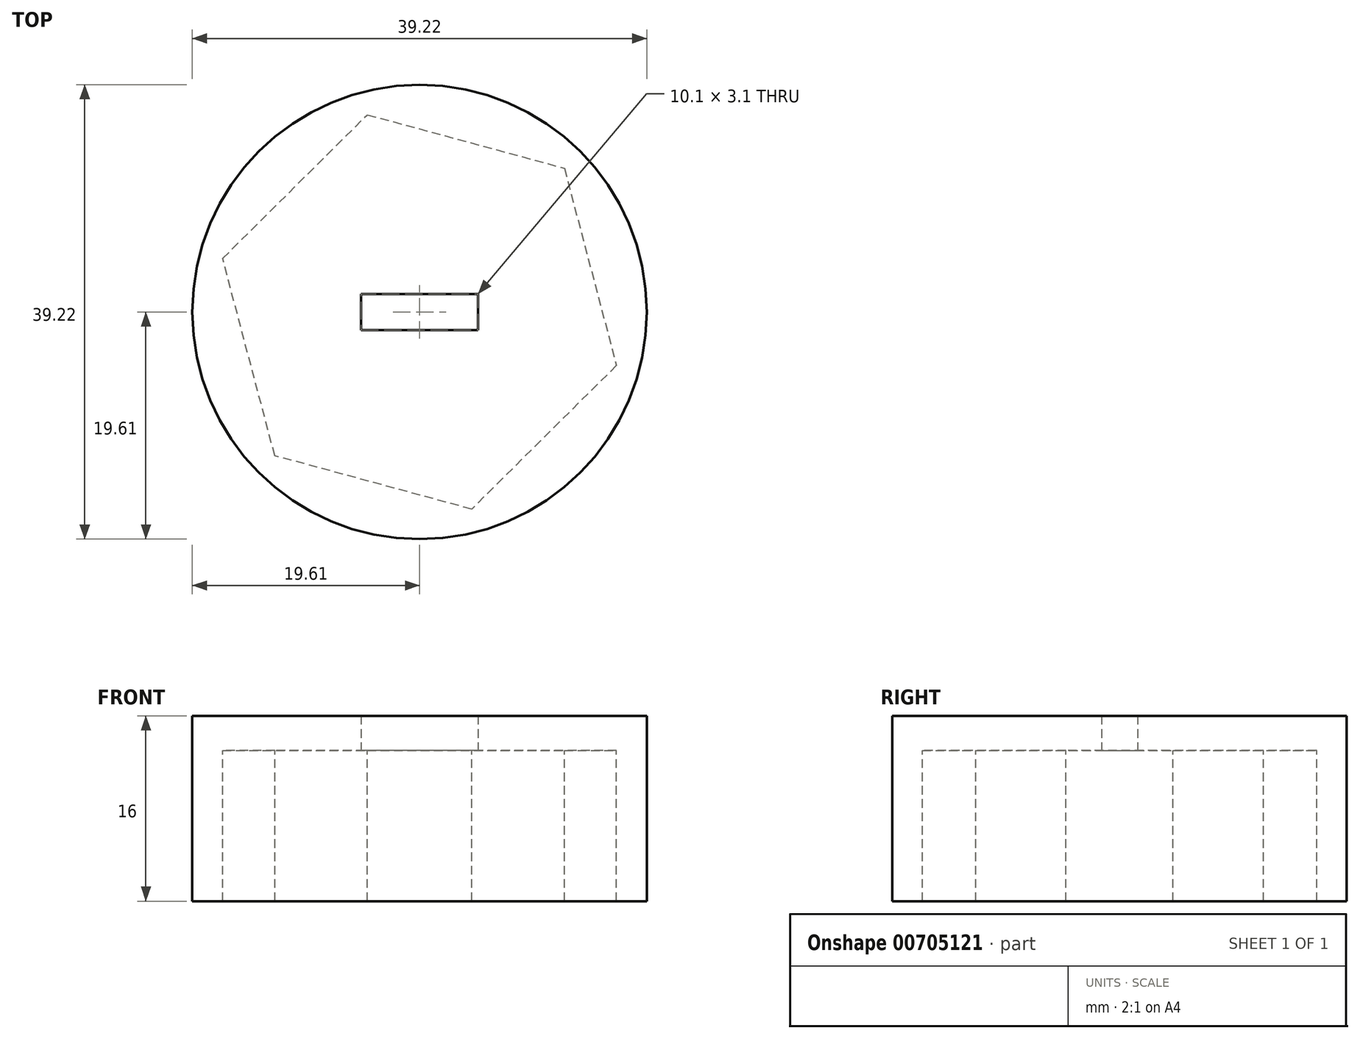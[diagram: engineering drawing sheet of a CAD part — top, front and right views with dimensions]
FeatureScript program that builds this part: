
annotation { "Feature Type Name" : "Feature", "Feature Type Description" : "" }
export const myFeature = defineFeature(function(context is Context, id is Id, definition is map)
    precondition{}
    {
        {
            var Q0;
            Q0=qCreatedBy(makeId("Top.planeOp"),FACE);
            var sketch = newSketch(context, id + "F0", { "sketchPlane" : qUnion([Q0])});
            skCircle(sketch, "E0", {"center": v(0, 0) * mm, "radius": 19.6 * mm});
            skLineSegment(sketch, "E1.bottom", {"start": v(5.05, -1.55) * mm, "end": v(-5.05, -1.55) * mm});
            skLineSegment(sketch, "E1.top", {"start": v(5.05, 1.55) * mm, "end": v(-5.05, 1.55) * mm});
            skLineSegment(sketch, "E1.left", {"start": v(5.05, -1.55) * mm, "end": v(5.05, 1.55) * mm});
            skLineSegment(sketch, "E1.right", {"start": v(-5.05, -1.55) * mm, "end": v(-5.05, 1.55) * mm});
            skCircle(sketch, "E2.cCircle", {"center": v(0, 0) * mm, "radius": 15.25 * mm, "construction": true});
            skLineSegment(sketch, "E2.0", {"start": v(-17, 4.62) * mm, "end": v(-4.5, 17.02) * mm});
            skLineSegment(sketch, "E2.1", {"start": v(-4.5, 17.02) * mm, "end": v(12.5, 12.4) * mm});
            skLineSegment(sketch, "E2.2", {"start": v(12.5, 12.4) * mm, "end": v(17, -4.62) * mm});
            skLineSegment(sketch, "E2.3", {"start": v(17, -4.62) * mm, "end": v(4.5, -17.02) * mm});
            skLineSegment(sketch, "E2.4", {"start": v(4.5, -17.02) * mm, "end": v(-12.5, -12.4) * mm});
            skLineSegment(sketch, "E2.5", {"start": v(-12.5, -12.4) * mm, "end": v(-17, 4.62) * mm});
            skPoint(sketch, "E2.0.midPoint", {"position": v(-10.75, 10.82) * mm});
            skSolve(sketch);
        }
        {
            var Q0;
            Q0=makeQuery(id+"F0.imprint","IMPRINT",FACE,{"disambiguationData":[TD([[makeQuery(id+"F0.imprint","IMPRINT",EDGE,{"derivedFrom":sQuery(id+"F0.wireOp",EDGE,"E0")}),1.0]])]});
            var Q1;
            Q1=makeQuery(id+"F0.imprint","IMPRINT",FACE,{"disambiguationData":[TD([[makeQuery(id+"F0.imprint","IMPRINT",EDGE,{"derivedFrom":sQuery(id+"F0.wireOp",EDGE,"E1.bottom")}),1.0]])]});
            extrude(context, id + "F1", {"entities" : qUnion([Q0, Q1]), "depth" : 3 * mm, "offsetDistance" : 25 * mm});
        }
        {
            var Q0;
            Q0=makeQuery(id+"F0.imprint","IMPRINT",FACE,{"disambiguationData":[TD([[makeQuery(id+"F0.imprint","IMPRINT",EDGE,{"derivedFrom":sQuery(id+"F0.wireOp",EDGE,"E0")}),1.0]])]});
            extrude(context, id + "F2", {"entities" : qUnion([Q0]), "operationType" : NewBodyOperationType.ADD, "oppositeDirection" : true, "depth" : 13 * mm, "offsetDistance" : 25 * mm});
        }
    });
